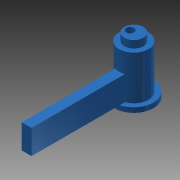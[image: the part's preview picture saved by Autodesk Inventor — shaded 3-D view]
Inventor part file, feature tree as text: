
AUTODESK INVENTOR PART (.ipt)
format: ipt  version: 2013 (Build 170138000, 138)  size: 109,568 bytes
history: native  units: mm
features: extrude x4, sketch x2
ambient origin geometry x8: Origin, YZ Plane, XZ Plane, XY Plane, X Axis, Y Axis, Z Axis, Center Point
bodies: Solid1 (feature_tree)
feature tree (6):
  extrude  "Extrusion1"  Depth=20.0mm TaperAngle=0.0deg
  extrude  "Extrusion2"  Depth=3.0mm TaperAngle=0.0deg
  extrude  "Extrusion3"  Depth=3.2mm
  extrude  "Extrusion5"  Depth=1.5mm
  sketch  "Sketch3"  dims[d1=12.0mm d2=20.0mm d3=0.0mm]
  sketch  "Sketch5"  dims[d4=7.8mm d5=3.0mm d6=0.0mm d8=3.2mm d9=1.5mm d10=16.0mm d11=2.0mm d12=0.0mm d22=40.0mm d24=10.0mm d25=4.0mm d26=0.0mm d27=4.0mm d28=0.0mm]
